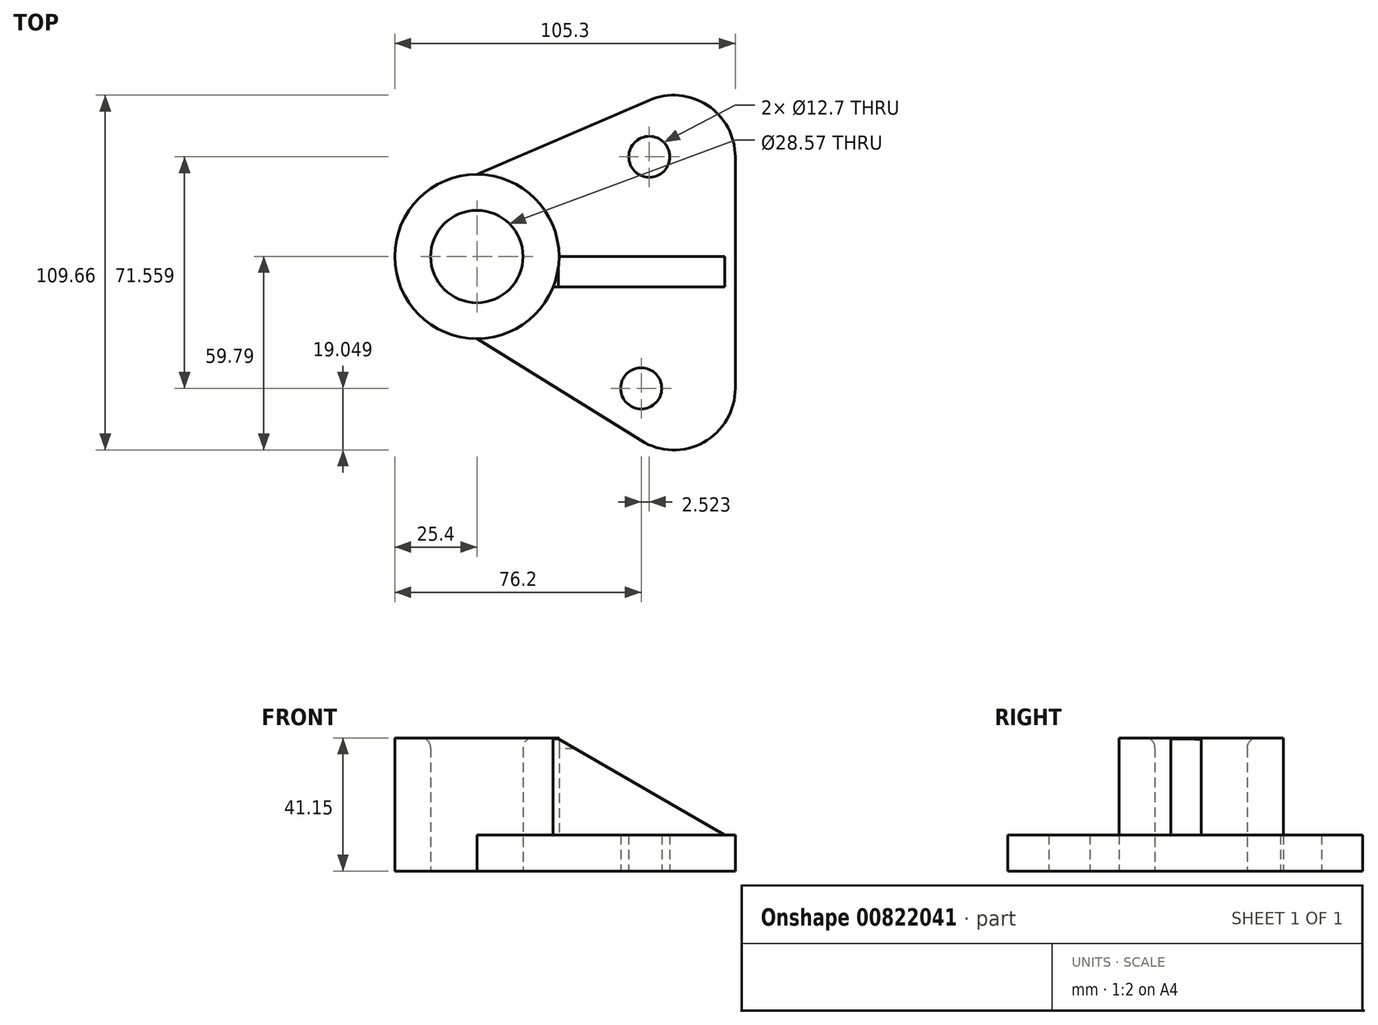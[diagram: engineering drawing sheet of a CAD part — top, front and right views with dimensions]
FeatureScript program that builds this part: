
annotation { "Feature Type Name" : "Feature", "Feature Type Description" : "" }
export const myFeature = defineFeature(function(context is Context, id is Id, definition is map)
    precondition{}
    {
        {
            var Q0;
            Q0=qCreatedBy(makeId("Top.planeOp"),FACE);
            var sketch = newSketch(context, id + "F0", { "sketchPlane" : qUnion([Q0])});
            skCircle(sketch, "E0", {"center": v(0, 0) * mm, "radius": 14.29 * mm});
            skCircle(sketch, "E1", {"center": v(0, 0) * mm, "radius": 25.4 * mm});
            skCircle(sketch, "E2", {"center": v(53.32, 30.82) * mm, "radius": 6.35 * mm});
            skCircle(sketch, "E3", {"center": v(50.8, -40.74) * mm, "radius": 6.35 * mm});
            skLineSegment(sketch, "E4", {"start": v(0, 25.4) * mm, "end": v(53.32, 48.32) * mm});
            skLineSegment(sketch, "E5", {"start": v(0, -25.4) * mm, "end": v(50.8, -56.93) * mm});
            skLineSegment(sketch, "E6", {"start": v(79.9, 30.82) * mm, "end": v(79.9, -40.74) * mm});
            skArc(sketch, "E7", {"start": v(79.9, 30.82) * mm, "mid": v(71.32, 46.73) * mm, "end": v(53.32, 48.32) * mm});
            skArc(sketch, "E8", {"start": v(50.8, -56.93) * mm, "mid": v(70.1, -57.39) * mm, "end": v(79.9, -40.74) * mm});
            skSolve(sketch);
        }
        {
            var Q0;
            Q0=makeQuery(id+"F0.imprint","IMPRINT",FACE,{"disambiguationData":[TD([[makeQuery(id+"F0.imprint","IMPRINT",EDGE,{"derivedFrom":sQuery(id+"F0.wireOp",EDGE,"E0")}),-1.0]])]});
            extrude(context, id + "F1", {"entities" : qUnion([Q0]), "depth" : 41.15 * mm, "offsetDistance" : 25.4 * mm});
        }
        {
            var Q0;
            Q0=makeQuery(id+"F0.imprint","IMPRINT",FACE,{"disambiguationData":[TD([[makeQuery(id+"F0.imprint","IMPRINT",EDGE,{"derivedFrom":sQuery(id+"F0.wireOp",EDGE,"E2")}),-1.0]])]});
            extrude(context, id + "F2", {"entities" : qUnion([Q0]), "operationType" : NewBodyOperationType.ADD, "depth" : 11.18 * mm, "offsetDistance" : 25.4 * mm});
        }
        {
            var Q0;
            Q0=makeQuery(id+"F2.opExtrude","CAP_FACE",FACE,{"disambiguationData":[OSD([sQuery(id+"F0.wireOp",EDGE,"E1"),sQuery(id+"F0.wireOp",EDGE,"E2"),sQuery(id+"F0.wireOp",EDGE,"E3"),sQuery(id+"F0.wireOp",EDGE,"E4"),sQuery(id+"F0.wireOp",EDGE,"E5"),sQuery(id+"F0.wireOp",EDGE,"E6"),sQuery(id+"F0.wireOp",EDGE,"E7"),sQuery(id+"F0.wireOp",EDGE,"E8")])],"isStart":false});
            var sketch = newSketch(context, id + "F3", { "sketchPlane" : qUnion([Q0])});
            skLineSegment(sketch, "E9", {"start": v(76.6, 0) * mm, "end": v(25.4, 0) * mm});
            skLineSegment(sketch, "E10", {"start": v(76.6, 0) * mm, "end": v(76.6, -9.37) * mm});
            skLineSegment(sketch, "E11", {"start": v(76.6, -9.37) * mm, "end": v(23.6, -9.37) * mm});
            skSolve(sketch);
        }
        {
            var Q0;
            Q0 = qSketchRegion(id + "F3", true);
            var Q1;
            {var subQ0=sQuery(id+"F3.wireOp",EDGE,"E9");Q1=makeQuery(id+"F3.imprint","IMPRINT",FACE,{"disambiguationData":[TD([[makeQuery(id+"F3.imprint","IMPRINT",EDGE,{"derivedFrom":subQ0}),1.0]])]});}
            extrude(context, id + "F4", {"entities" : qUnion([Q0, Q1]), "operationType" : NewBodyOperationType.ADD, "depth" : 26.67 * mm, "offsetDistance" : 25.4 * mm});
        }
        {
            var Q0;
            Q0=makeQuery(id+"F4.opExtrude","SWEPT_FACE",FACE,{"disambiguationData":[OSD([sQuery(id+"F3.wireOp",EDGE,"E11")])]});
            var sketch = newSketch(context, id + "F5", { "sketchPlane" : qUnion([Q0])});
            skLineSegment(sketch, "E12", {"start": v(25.22, 40.84) * mm, "end": v(76.6, 11.18) * mm});
            skLineSegment(sketch, "E13", {"start": v(25.22, 40.84) * mm, "end": v(23.6, 40.84) * mm});
            skLineSegment(sketch, "E14", {"start": v(23.6, 40.84) * mm, "end": v(23.6, 37.85) * mm});
            skSolve(sketch);
        }
        {
            var Q0;
            {var subQ1=sQuery(id+"F3.wireOp",EDGE,"E11");var subQ2=makeQuery(id+"F4.opExtrude","SWEPT_EDGE",EDGE,{"disambiguationData":[OSD([sQuery(id+"F3.wireOp",EDGE,"E10"),subQ1])]});Q0=makeQuery(id+"F5.imprint","IMPRINT",FACE,{"disambiguationData":[TD([[makeQuery(id+"F5.imprint","IMPRINT",EDGE,{"derivedFrom":subQ2}),-1.0]])]});}
            extrude(context, id + "F6", {"entities" : qUnion([Q0]), "operationType" : NewBodyOperationType.REMOVE, "oppositeDirection" : true, "depth" : 25.4 * mm, "offsetDistance" : 25.4 * mm});
        }
        {
            var Q0;
            {var subQ0=sQuery(id+"F5.wireOp",EDGE,"E13");Q0=makeQuery(id+"F5.imprint","IMPRINT",FACE,{"disambiguationData":[TD([[makeQuery(id+"F5.imprint","IMPRINT",EDGE,{"derivedFrom":subQ0}),1.0]])]});}
            extrude(context, id + "F7", {"entities" : qUnion([Q0]), "operationType" : NewBodyOperationType.ADD, "oppositeDirection" : true, "depth" : 9.4 * mm, "offsetDistance" : 25.4 * mm});
        }
        {
            var Q0;
            Q0=makeQuery(id+"F4.opExtrude","CAP_EDGE",EDGE,{"disambiguationData":[OSD([sQuery(id+"F3.wireOp",EDGE,"E9")])],"isStart":true});
            var Q1;
            {var subQ0=sQuery(id+"F0.wireOp",EDGE,"E1");var subQ1=sQuery(id+"F0.wireOp",EDGE,"E4");Q1=makeQuery(id+"F4.boolean.opBoolean","SPLIT",EDGE,{"disambiguationData":[TD([makeQuery(id+"F2.opExtrude","SWEPT_FACE",FACE,{"disambiguationData":[OSD([subQ1])]})])],"derivedFrom":makeQuery(id+"F2.opExtrude","CAP_EDGE",EDGE,{"disambiguationData":[OSD([subQ0])],"isStart":false})});}
            var Q2;
            Q2=makeQuery(id+"F4.opExtrude","CAP_EDGE",EDGE,{"disambiguationData":[OSD([sQuery(id+"F3.wireOp",EDGE,"E11")])],"isStart":true});
            var Q3;
            {var subQ0=sQuery(id+"F0.wireOp",EDGE,"E1");var subQ1=sQuery(id+"F0.wireOp",EDGE,"E5");Q3=makeQuery(id+"F4.boolean.opBoolean","SPLIT",EDGE,{"disambiguationData":[TD([makeQuery(id+"F2.opExtrude","SWEPT_FACE",FACE,{"disambiguationData":[OSD([subQ1])]})])],"derivedFrom":makeQuery(id+"F2.opExtrude","CAP_EDGE",EDGE,{"disambiguationData":[OSD([subQ0])],"isStart":false})});}
            var Q4;
            Q4=makeQuery(id+"F1.opExtrude","CAP_EDGE",EDGE,{"disambiguationData":[OSD([sQuery(id+"F0.wireOp",EDGE,"E0")])],"isStart":false});
            fillet(context, id + "F8", {"entities" : qUnion([Q0, Q1, Q2, Q3, Q4]), "radius" : 3.05 * mm, "tangentPropagation" : true, "allowEdgeOverflow" : false});
        }
    });
